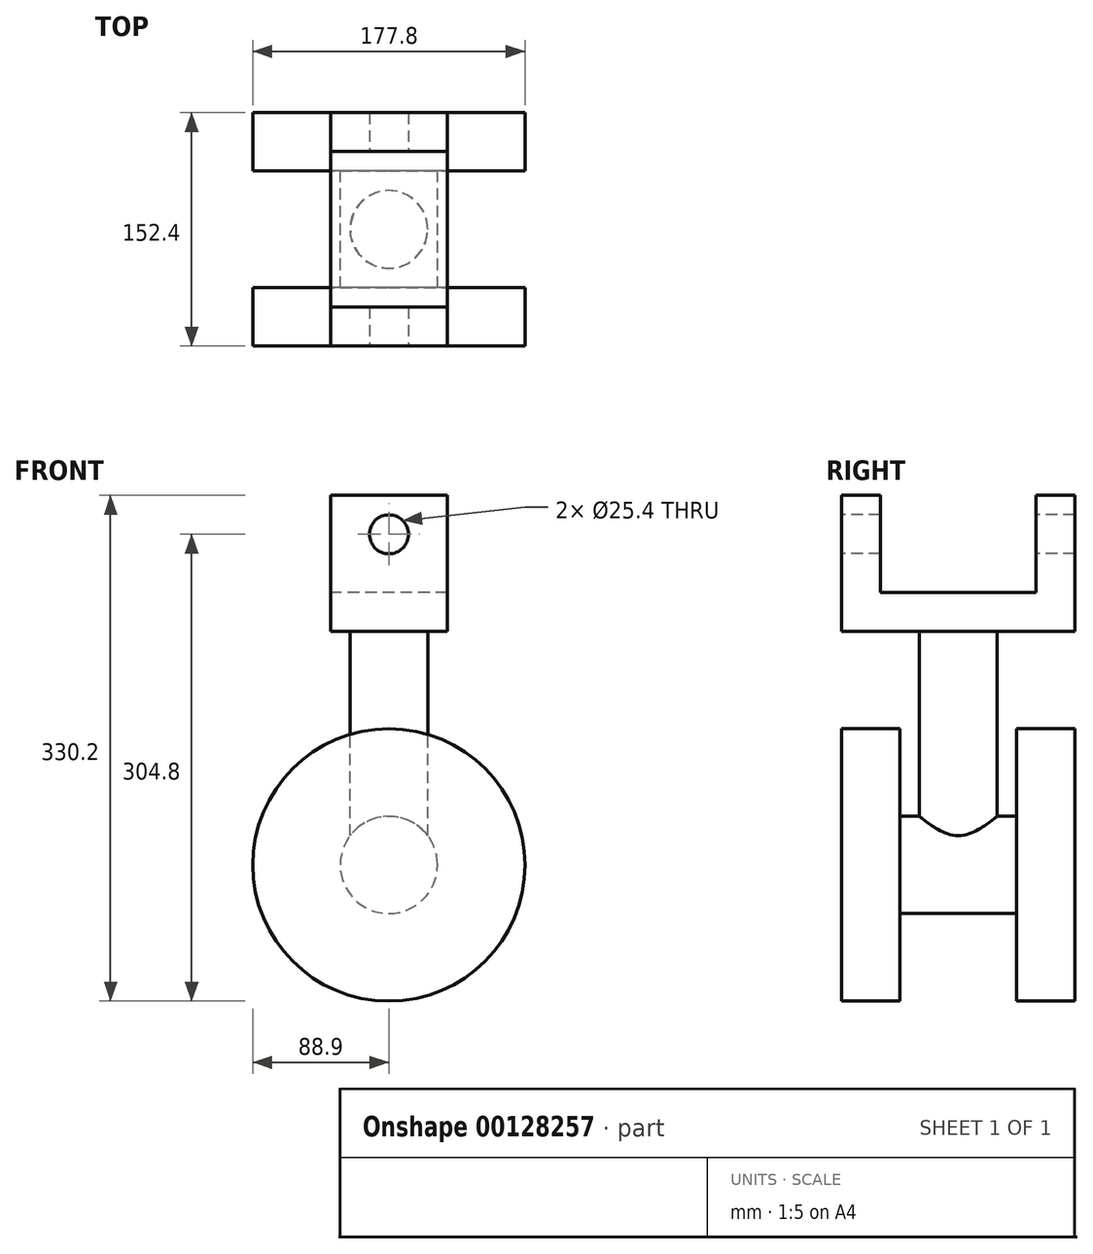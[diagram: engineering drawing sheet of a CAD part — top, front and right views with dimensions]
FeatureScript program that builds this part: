
annotation { "Feature Type Name" : "Feature", "Feature Type Description" : "" }
export const myFeature = defineFeature(function(context is Context, id is Id, definition is map)
    precondition{}
    {
        {
            var Q0;
            Q0=qCreatedBy(makeId("Top.planeOp"),FACE);
            var sketch = newSketch(context, id + "F0", { "sketchPlane" : qUnion([Q0])});
            skCircle(sketch, "E0", {"center": v(0, 0) * mm, "radius": 25.4 * mm});
            skSolve(sketch);
        }
        {
            var Q0;
            Q0=makeQuery(id+"F0.imprint","IMPRINT",FACE,{"disambiguationData":[TD([[makeQuery(id+"F0.imprint","IMPRINT",EDGE,{"derivedFrom":sQuery(id+"F0.wireOp",EDGE,"E0")}),1.0]])]});
            extrude(context, id + "F1", {"entities" : qUnion([Q0]), "oppositeDirection" : true, "depth" : 152.4 * mm});
        }
        {
            var Q0;
            Q0=qCreatedBy(makeId("Right.planeOp"),FACE);
            var sketch = newSketch(context, id + "F2", { "sketchPlane" : qUnion([Q0])});
            skLineSegment(sketch, "E1", {"start": v(0, 0) * mm, "end": v(0, 71.61) * mm, "construction": true});
            skLineSegment(sketch, "E2", {"start": v(0, 25.4) * mm, "end": v(50.8, 25.4) * mm});
            skLineSegment(sketch, "E3", {"start": v(50.8, 25.4) * mm, "end": v(50.8, 88.9) * mm});
            skLineSegment(sketch, "E4", {"start": v(50.8, 88.9) * mm, "end": v(76.2, 88.9) * mm});
            skLineSegment(sketch, "E5", {"start": v(76.2, 88.9) * mm, "end": v(76.2, 0) * mm});
            skLineSegment(sketch, "E6", {"start": v(76.2, 0) * mm, "end": v(0, 0) * mm});
            skLineSegment(sketch, "E7", {"start": v(50.8, 25.4) * mm, "end": v(50.8, 0) * mm, "construction": true});
            skLineSegment(sketch, "E8.MirrorCS", {"start": v(-76.2, 0) * mm, "end": v(0, 0) * mm});
            skLineSegment(sketch, "E9.MirrorCS", {"start": v(-76.2, 88.9) * mm, "end": v(-76.2, 0) * mm});
            skLineSegment(sketch, "E10.MirrorCS", {"start": v(-50.8, 88.9) * mm, "end": v(-76.2, 88.9) * mm});
            skLineSegment(sketch, "E11.MirrorCS", {"start": v(0, 25.4) * mm, "end": v(-50.8, 25.4) * mm});
            skLineSegment(sketch, "E12.MirrorCS", {"start": v(-50.8, 25.4) * mm, "end": v(-50.8, 88.9) * mm});
            skSolve(sketch);
        }
        {
            var Q0;
            Q0 = qSketchRegion(id + "F2", true);
            extrude(context, id + "F3", {"entities" : qUnion([Q0]), "operationType" : NewBodyOperationType.ADD, "endBound" : BoundingType.SYMMETRIC, "depth" : 76.2 * mm});
        }
        {
            var Q0;
            Q0=qCreatedBy(makeId("Front.planeOp"),FACE);
            var sketch = newSketch(context, id + "F4", { "sketchPlane" : qUnion([Q0])});
            skLineSegment(sketch, "E13.0", {"start": v(-25.4, -152.4) * mm, "end": v(25.4, -152.4) * mm, "construction": true});
            skCircle(sketch, "E14", {"center": v(0, -152.4) * mm, "radius": 31.75 * mm});
            skSolve(sketch);
        }
        {
            var Q0;
            Q0=makeQuery(id+"F4.imprint","IMPRINT",FACE,{"disambiguationData":[TD([[makeQuery(id+"F4.imprint","IMPRINT",EDGE,{"derivedFrom":sQuery(id+"F4.wireOp",EDGE,"E14")}),1.0]])]});
            extrude(context, id + "F5", {"entities" : qUnion([Q0]), "operationType" : NewBodyOperationType.ADD, "endBound" : BoundingType.SYMMETRIC, "depth" : 76.2 * mm});
        }
        {
            var Q0;
            Q0=makeQuery(id+"F5.opExtrude","CAP_FACE",FACE,{"disambiguationData":[OSD([sQuery(id+"F4.wireOp",EDGE,"E14")])],"isStart":false});
            var sketch = newSketch(context, id + "F6", { "sketchPlane" : qUnion([Q0])});
            skCircle(sketch, "E15.0", {"center": v(0, -152.4) * mm, "radius": 31.75 * mm, "construction": true});
            skCircle(sketch, "E16", {"center": v(0, -152.4) * mm, "radius": 88.9 * mm});
            skSolve(sketch);
        }
        {
            var Q0;
            Q0 = qSketchRegion(id + "F6", true);
            extrude(context, id + "F7", {"entities" : qUnion([Q0]), "operationType" : NewBodyOperationType.ADD, "depth" : 38.1 * mm});
        }
        {
            var Q0;
            Q0=makeQuery(id+"F1.opExtrude","SWEPT_BODY",BODY,{"disambiguationData":[OSD([sQuery(id+"F0.wireOp",EDGE,"E0")])]});
            var Q1;
            Q1=qCreatedBy(makeId("Front.planeOp"),FACE);
            mirror(context, id + "F8", {"operationType" : NewBodyOperationType.ADD, "entities" : qUnion([Q0]), "mirrorPlane" : qUnion([Q1])});
        }
        {
            var Q0;
            Q0=makeQuery(id+"F3.opExtrude","SWEPT_FACE",FACE,{"disambiguationData":[OSD([sQuery(id+"F2.wireOp",EDGE,"E9.MirrorCS")])]});
            var sketch = newSketch(context, id + "F9", { "sketchPlane" : qUnion([Q0])});
            skLineSegment(sketch, "E17", {"start": v(0, 88.9) * mm, "end": v(0, 63.5) * mm, "construction": true});
            skPoint(sketch, "E17.endSnap0", {"position": v(0, 88.9) * mm});
            skCircle(sketch, "E18", {"center": v(0, 63.5) * mm, "radius": 12.7 * mm});
            skSolve(sketch);
        }
        {
            var Q0;
            Q0 = qSketchRegion(id + "F9", true);
            extrude(context, id + "F10", {"entities" : qUnion([Q0]), "operationType" : NewBodyOperationType.REMOVE, "endBound" : BoundingType.THROUGH_ALL, "oppositeDirection" : true, "depth" : 25.4 * mm});
        }
    });
